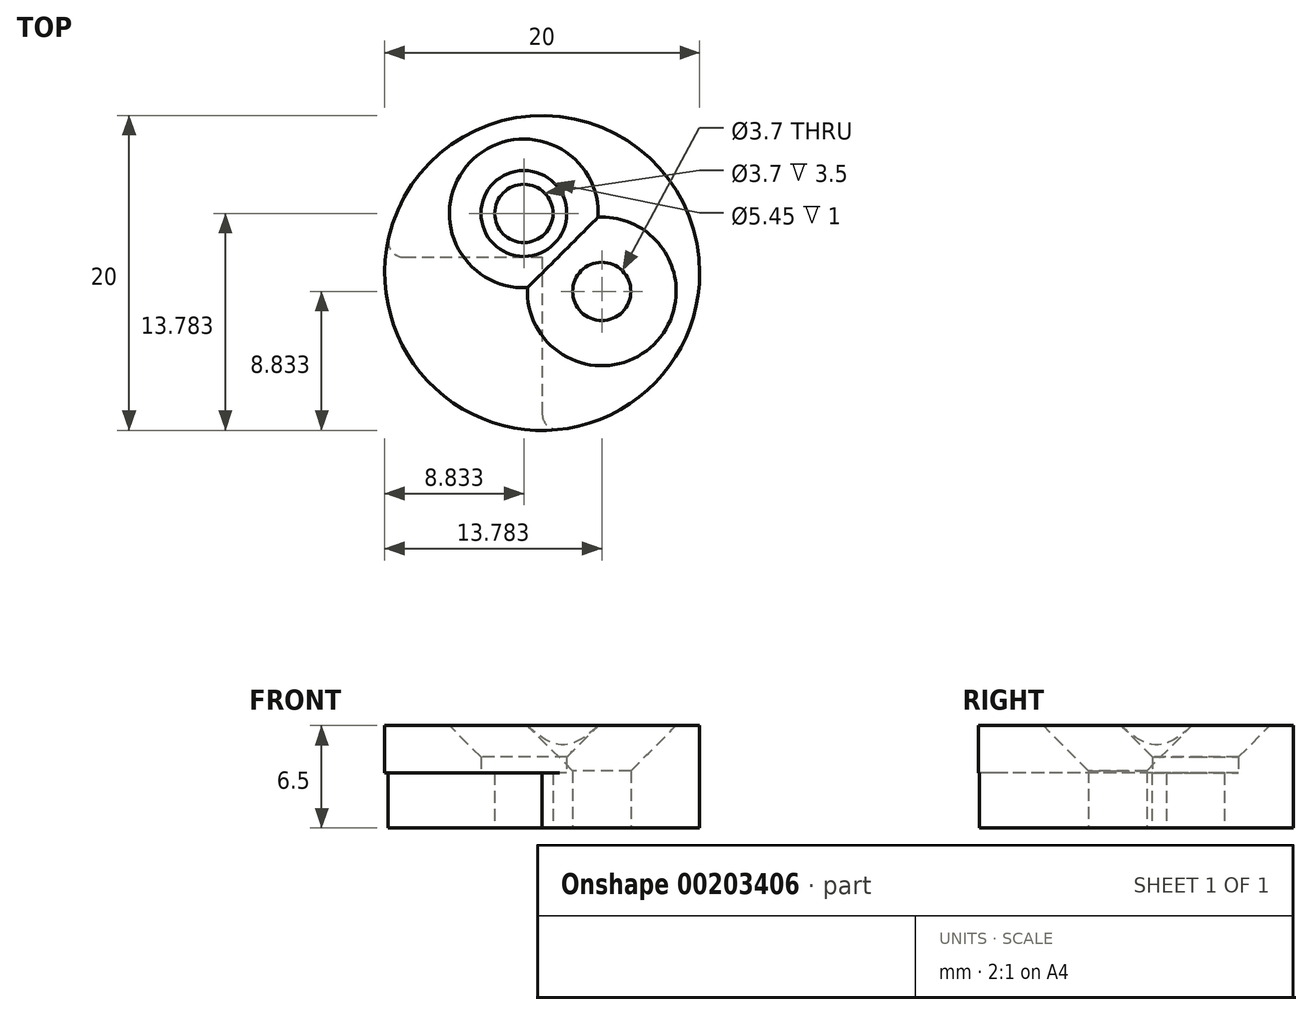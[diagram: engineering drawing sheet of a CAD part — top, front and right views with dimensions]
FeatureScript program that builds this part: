
annotation { "Feature Type Name" : "Feature", "Feature Type Description" : "" }
export const myFeature = defineFeature(function(context is Context, id is Id, definition is map)
    precondition{}
    {
        {
            var Q0;
            Q0=qCreatedBy(makeId("Top.planeOp"),FACE);
            var sketch = newSketch(context, id + "F0", { "sketchPlane" : qUnion([Q0])});
            skArc(sketch, "E0", {"start": v(0, -10) * mm, "mid": v(7.42, 6.7) * mm, "end": v(-9.95, 1) * mm});
            skLineSegment(sketch, "E1", {"start": v(-9.95, 1) * mm, "end": v(0, 1) * mm});
            skLineSegment(sketch, "E2", {"start": v(0, 1) * mm, "end": v(0, -10) * mm});
            skCircle(sketch, "E3", {"center": v(3.78, -1.17) * mm, "radius": 1.85 * mm});
            skCircle(sketch, "E4", {"center": v(-1.17, 3.78) * mm, "radius": 1.85 * mm});
            skLineSegment(sketch, "E5", {"start": v(-9.85, 9.85) * mm, "end": v(10.87, -10.87) * mm, "construction": true});
            skLineSegment(sketch, "E6", {"start": v(-1.17, 3.78) * mm, "end": v(3.78, -1.17) * mm, "construction": true});
            skLineSegment(sketch, "E7", {"start": v(1.3, 1.3) * mm, "end": v(0, 0) * mm, "construction": true});
            skSolve(sketch);
        }
        {
            var Q0;
            Q0=qSketchRegion(id+"F0",true);
            extrude(context, id + "F1", {"entities" : qUnion([Q0]), "depth" : 3.5 * mm});
        }
        {
            var Q0;
            Q0=makeQuery(id+"F1.opExtrude","CAP_FACE",FACE,{"disambiguationData":[OSD([sQuery(id+"F0.wireOp",EDGE,"E0"),sQuery(id+"F0.wireOp",EDGE,"E1"),sQuery(id+"F0.wireOp",EDGE,"E2"),sQuery(id+"F0.wireOp",EDGE,"E3"),sQuery(id+"F0.wireOp",EDGE,"E4")])],"isStart":false});
            var sketch = newSketch(context, id + "F2", { "sketchPlane" : qUnion([Q0])});
            skCircle(sketch, "E8", {"center": v(0, 0) * mm, "radius": 10 * mm});
            skCircle(sketch, "E9", {"center": v(3.78, -1.17) * mm, "radius": 2.72 * mm});
            skCircle(sketch, "E10", {"center": v(-1.17, 3.78) * mm, "radius": 2.72 * mm});
            skSolve(sketch);
        }
        {
            var Q0;
            Q0=qSketchRegion(id+"F2",true);
            extrude(context, id + "F3", {"entities" : qUnion([Q0]), "operationType" : NewBodyOperationType.ADD, "depth" : 3 * mm});
        }
        {
            var Q0;
            Q0=makeQuery(id+"F3.opExtrude","CAP_EDGE",EDGE,{"disambiguationData":[OSD([sQuery(id+"F2.wireOp",EDGE,"E10")])],"isStart":true});
            var Q1;
            Q1=makeQuery(id+"F3.opExtrude","CAP_EDGE",EDGE,{"disambiguationData":[OSD([sQuery(id+"F2.wireOp",EDGE,"E9")])],"isStart":true});
            chamfer(context, id + "F4", {"entities" : qUnion([Q0, Q1]), "width" : 1 * mm, "tangentPropagation" : true});
        }
        {
            var Q0;
            Q0=makeQuery(id+"F3.opExtrude","CAP_EDGE",EDGE,{"disambiguationData":[OSD([sQuery(id+"F2.wireOp",EDGE,"E10")])],"isStart":false});
            var Q1;
            Q1=makeQuery(id+"F3.opExtrude","CAP_EDGE",EDGE,{"disambiguationData":[OSD([sQuery(id+"F2.wireOp",EDGE,"E9")])],"isStart":false});
            chamfer(context, id + "F5", {"entities" : qUnion([Q0, Q1]), "width" : 2 * mm, "tangentPropagation" : true});
        }
        {
            var Q0;
            Q0=makeQuery(id+"F1.opExtrude","SWEPT_EDGE",EDGE,{"disambiguationData":[OSD([sQuery(id+"F0.wireOp",EDGE,"E0"),sQuery(id+"F0.wireOp",EDGE,"E2")])]});
            var Q1;
            Q1=makeQuery(id+"F1.opExtrude","SWEPT_EDGE",EDGE,{"disambiguationData":[OSD([sQuery(id+"F0.wireOp",EDGE,"E0"),sQuery(id+"F0.wireOp",EDGE,"E1")])]});
            fillet(context, id + "F6", {"entities" : qUnion([Q0, Q1]), "radius" : 1 * mm, "tangentPropagation" : true, "allowEdgeOverflow" : false});
        }
    });
